# Revit family: Regenrohrschelle
name_source: partatom
category: Generic Models
revit_build: Autodesk Revit 2015 (Build: 20140606_1530(x64)
units: mm (PartAtom-declared; Revit-internal decimal feet)

## types (9) — shared parameters
Manufacturer = OBO Bettermann
SW = 13 mm
URL = http://www.obo-bettermann.com

## per-type parameters (varying)
| type | GTIN | Manufacturer Art.No. | Material | Radius | Radius 1 | Width | Width 1 |
| 301 DIN-80 | 4012195425595 | 5350085 | Strip-galvanised | 40 mm  [stored 0.131234 ft] | 41 mm  [stored 0.134514 ft] | 41 mm  [stored 0.134514 ft] | 38 mm  [stored 0.124672 ft] |
| 301 DIN-90 | 4012195425656 | 5350093 | Strip-galvanised | 45 mm  [stored 0.147638 ft] | 46 mm  [stored 0.150919 ft] | 46 mm  [stored 0.150919 ft] | 44 mm  [stored 0.144357 ft] |
| 301 DIN-100 | 4012195425717 | 5350107 | Strip-galvanised | 50 mm  [stored 0.164042 ft] | 51 mm  [stored 0.167323 ft] | 51 mm  [stored 0.167323 ft] | 48 mm  [stored 0.15748 ft] |
| 301 DIN-110 | 4012195425779 | 5350115 | Strip-galvanised | 55 mm  [stored 0.180446 ft] | 57 mm | 56 mm | 53 mm  [stored 0.173885 ft] |
| 301 DIN-120 | 4012195425830 | 5350123 | Strip-galvanised | 60 mm  [stored 0.19685 ft] | 62 mm | 61 mm | 58 mm  [stored 0.190289 ft] |
| 301 CU-80 | 4012195426257 | 5350689 | Copper | 40 mm  [stored 0.131234 ft] | 41 mm  [stored 0.134514 ft] | 41 mm  [stored 0.134514 ft] | 38 mm  [stored 0.124672 ft] |
| 301 CU-100 | 4012195426370 | 5350700 | Copper | 50 mm  [stored 0.164042 ft] | 51 mm  [stored 0.167323 ft] | 51 mm  [stored 0.167323 ft] | 48 mm  [stored 0.15748 ft] |
| 301 CU-110 | 4012195426431 | 5350719 | Copper | 55 mm  [stored 0.180446 ft] | 57 mm | 56 mm | 53 mm  [stored 0.173885 ft] |
| 301 CU-120 | 4012195426493 | 5350727 | Copper | 60 mm  [stored 0.19685 ft] | 62 mm | 61 mm | 58 mm  [stored 0.190289 ft] |

note: column(s) folded — value = type name in every type: Article Type

note: [stored X ft] marks values corroborated as IEEE doubles in the binary element streams (Revit-internal decimal feet)

## geometry (parser evidence)
native form markers: Sweep x2
no freeform markers — native parametric forms only
